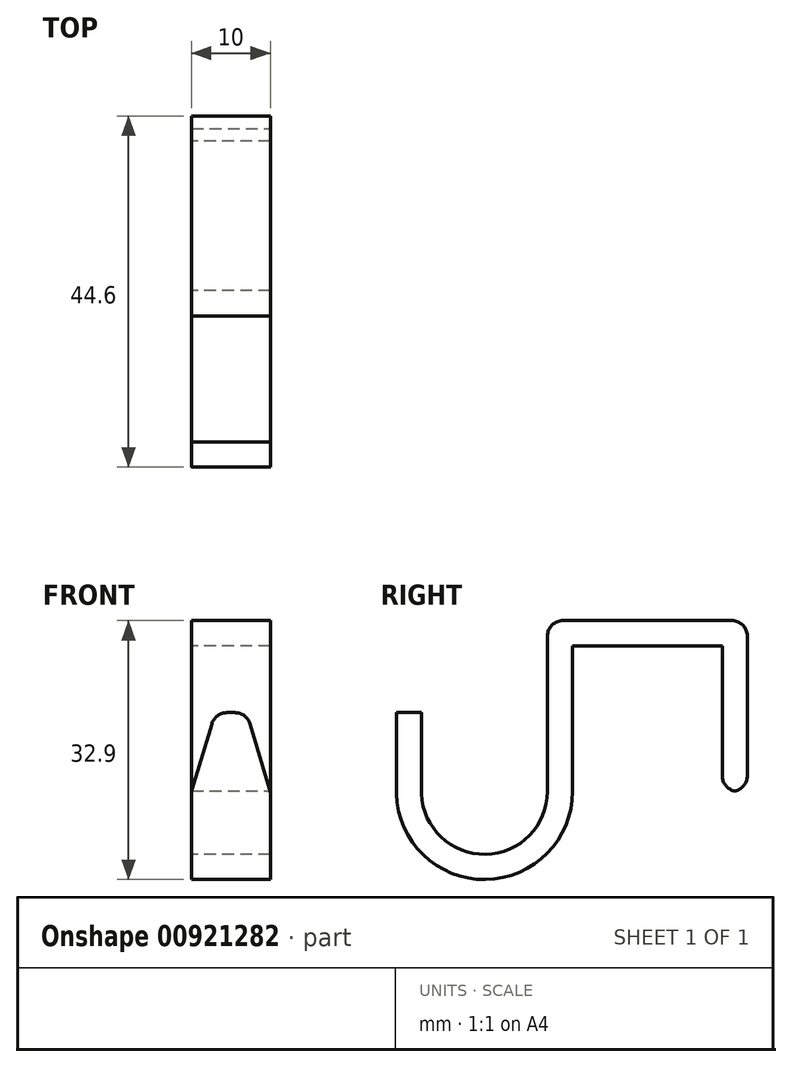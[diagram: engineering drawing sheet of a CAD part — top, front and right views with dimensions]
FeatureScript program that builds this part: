
annotation { "Feature Type Name" : "Feature", "Feature Type Description" : "" }
export const myFeature = defineFeature(function(context is Context, id is Id, definition is map)
    precondition{}
    {
        {
            var Q0;
            Q0=qCreatedBy(makeId("Right.planeOp"),FACE);
            var sketch = newSketch(context, id + "F0", { "sketchPlane" : qUnion([Q0])});
            skLineSegment(sketch, "E0.bottom", {"start": v(-12.7, 0) * mm, "end": v(12.7, 0) * mm});
            skLineSegment(sketch, "E0.top", {"start": v(-12.7, 21.7) * mm, "end": v(12.7, 21.7) * mm});
            skLineSegment(sketch, "E0.left", {"start": v(-12.7, 0) * mm, "end": v(-12.7, 21.7) * mm});
            skLineSegment(sketch, "E0.right", {"start": v(12.7, 0) * mm, "end": v(12.7, 21.7) * mm});
            skLineSegment(sketch, "E1.bottom", {"start": v(-9.5, 0) * mm, "end": v(9.5, 0) * mm});
            skLineSegment(sketch, "E1.top", {"start": v(-9.5, 18.5) * mm, "end": v(9.5, 18.5) * mm});
            skLineSegment(sketch, "E1.left", {"start": v(-9.5, 0) * mm, "end": v(-9.5, 18.5) * mm});
            skLineSegment(sketch, "E1.right", {"start": v(9.5, 0) * mm, "end": v(9.5, 18.5) * mm});
            skArc(sketch, "E2", {"start": v(-31.9, 0) * mm, "mid": v(-20.7, -11.2) * mm, "end": v(-9.5, 0) * mm});
            skArc(sketch, "E3", {"start": v(-28.7, 0) * mm, "mid": v(-20.7, -8) * mm, "end": v(-12.7, 0) * mm});
            skLineSegment(sketch, "E4", {"start": v(-31.9, 0) * mm, "end": v(-28.7, 0) * mm});
            skLineSegment(sketch, "E5.top", {"start": v(-31.9, 10) * mm, "end": v(-28.7, 10) * mm});
            skLineSegment(sketch, "E5.left", {"start": v(-31.9, 0) * mm, "end": v(-31.9, 10) * mm});
            skLineSegment(sketch, "E5.right", {"start": v(-28.7, 0) * mm, "end": v(-28.7, 10) * mm});
            skSolve(sketch);
        }
        {
            var Q0;
            Q0=makeQuery(id+"F0.imprint","IMPRINT",FACE,{"disambiguationData":[TD([[makeQuery(id+"F0.imprint","IMPRINT",EDGE,{"derivedFrom":sQuery(id+"F0.wireOp",EDGE,"E4")}),1.0]])]});
            var Q1;
            {var subQ2=sQuery(id+"F0.wireOp",EDGE,"E2");Q1=makeQuery(id+"F0.imprint","IMPRINT",FACE,{"disambiguationData":[TD([[makeQuery(id+"F0.imprint","IMPRINT",EDGE,{"derivedFrom":subQ2}),1.0]])]});}
            var Q2;
            Q2=makeQuery(id+"F0.imprint","IMPRINT",FACE,{"disambiguationData":[TD([[makeQuery(id+"F0.imprint","IMPRINT",EDGE,{"derivedFrom":sQuery(id+"F0.wireOp",EDGE,"E0.top")}),-1.0]])]});
            extrude(context, id + "F1", {"entities" : qUnion([Q0, Q1, Q2]), "depth" : 10 * mm, "offsetDistance" : 25 * mm});
        }
        {
            var Q0;
            Q0=makeQuery(id+"F1.opExtrude","CAP_EDGE",EDGE,{"disambiguationData":[OSD([sQuery(id+"F0.wireOp",EDGE,"E5.top")])],"isStart":false});
            var Q1;
            Q1=makeQuery(id+"F1.opExtrude","CAP_EDGE",EDGE,{"disambiguationData":[OSD([sQuery(id+"F0.wireOp",EDGE,"E5.top")])],"isStart":true});
            chamfer(context, id + "F2", {"entities" : qUnion([Q0, Q1]), "chamferType" : ChamferType.TWO_OFFSETS, "width1" : 3 * mm, "oppositeDirection" : false, "width2" : 10 * mm});
        }
        {
            var Q0;
            {var subQ0=sQuery(id+"F0.wireOp",EDGE,"E5.top");Q0=makeQuery(id+"F2.opChamfer","BLEND_EDGE",EDGE,{"blendedFrom":[makeQuery(id+"F1.opExtrude","CAP_EDGE",EDGE,{"disambiguationData":[OSD([subQ0])],"isStart":false}),makeQuery(id+"F1.opExtrude","SWEPT_FACE",FACE,{"disambiguationData":[OSD([subQ0])]})],"blendedInto":[makeQuery(id+"F1.opExtrude","SWEPT_FACE",FACE,{"disambiguationData":[OSD([subQ0])]})]});}
            var Q1;
            {var subQ0=sQuery(id+"F0.wireOp",EDGE,"E5.top");Q1=makeQuery(id+"F2.opChamfer","BLEND_EDGE",EDGE,{"blendedFrom":[makeQuery(id+"F1.opExtrude","CAP_EDGE",EDGE,{"disambiguationData":[OSD([subQ0])],"isStart":true}),makeQuery(id+"F1.opExtrude","SWEPT_FACE",FACE,{"disambiguationData":[OSD([subQ0])]})],"blendedInto":[makeQuery(id+"F1.opExtrude","SWEPT_FACE",FACE,{"disambiguationData":[OSD([subQ0])]})]});}
            var Q2;
            {var subQ0=sQuery(id+"F0.wireOp",EDGE,"E5.top");Q2=makeQuery(id+"F2.opChamfer","BLEND_EDGE",EDGE,{"blendedFrom":[makeQuery(id+"F1.opExtrude","CAP_EDGE",EDGE,{"disambiguationData":[OSD([subQ0])],"isStart":false}),makeQuery(id+"F1.opExtrude","CAP_FACE",FACE,{"disambiguationData":[OSD([sQuery(id+"F0.wireOp",EDGE,"E0.bottom"),sQuery(id+"F0.wireOp",EDGE,"E0.top"),sQuery(id+"F0.wireOp",EDGE,"E0.left"),sQuery(id+"F0.wireOp",EDGE,"E0.right"),sQuery(id+"F0.wireOp",EDGE,"E1.top"),sQuery(id+"F0.wireOp",EDGE,"E1.left"),sQuery(id+"F0.wireOp",EDGE,"E1.right"),sQuery(id+"F0.wireOp",EDGE,"E2"),sQuery(id+"F0.wireOp",EDGE,"E3"),subQ0,sQuery(id+"F0.wireOp",EDGE,"E5.left"),sQuery(id+"F0.wireOp",EDGE,"E5.right")])],"isStart":false})],"blendedInto":[makeQuery(id+"F1.opExtrude","CAP_FACE",FACE,{"disambiguationData":[OSD([sQuery(id+"F0.wireOp",EDGE,"E0.bottom"),sQuery(id+"F0.wireOp",EDGE,"E0.top"),sQuery(id+"F0.wireOp",EDGE,"E0.left"),sQuery(id+"F0.wireOp",EDGE,"E0.right"),sQuery(id+"F0.wireOp",EDGE,"E1.top"),sQuery(id+"F0.wireOp",EDGE,"E1.left"),sQuery(id+"F0.wireOp",EDGE,"E1.right"),sQuery(id+"F0.wireOp",EDGE,"E2"),sQuery(id+"F0.wireOp",EDGE,"E3"),subQ0,sQuery(id+"F0.wireOp",EDGE,"E5.left"),sQuery(id+"F0.wireOp",EDGE,"E5.right")])],"isStart":false})]});}
            var Q3;
            {var subQ0=sQuery(id+"F0.wireOp",EDGE,"E5.top");Q3=makeQuery(id+"F2.opChamfer","BLEND_EDGE",EDGE,{"blendedFrom":[makeQuery(id+"F1.opExtrude","CAP_EDGE",EDGE,{"disambiguationData":[OSD([subQ0])],"isStart":true}),makeQuery(id+"F1.opExtrude","CAP_FACE",FACE,{"disambiguationData":[OSD([sQuery(id+"F0.wireOp",EDGE,"E0.bottom"),sQuery(id+"F0.wireOp",EDGE,"E0.top"),sQuery(id+"F0.wireOp",EDGE,"E0.left"),sQuery(id+"F0.wireOp",EDGE,"E0.right"),sQuery(id+"F0.wireOp",EDGE,"E1.top"),sQuery(id+"F0.wireOp",EDGE,"E1.left"),sQuery(id+"F0.wireOp",EDGE,"E1.right"),sQuery(id+"F0.wireOp",EDGE,"E2"),sQuery(id+"F0.wireOp",EDGE,"E3"),subQ0,sQuery(id+"F0.wireOp",EDGE,"E5.left"),sQuery(id+"F0.wireOp",EDGE,"E5.right")])],"isStart":true})],"blendedInto":[makeQuery(id+"F1.opExtrude","CAP_FACE",FACE,{"disambiguationData":[OSD([sQuery(id+"F0.wireOp",EDGE,"E0.bottom"),sQuery(id+"F0.wireOp",EDGE,"E0.top"),sQuery(id+"F0.wireOp",EDGE,"E0.left"),sQuery(id+"F0.wireOp",EDGE,"E0.right"),sQuery(id+"F0.wireOp",EDGE,"E1.top"),sQuery(id+"F0.wireOp",EDGE,"E1.left"),sQuery(id+"F0.wireOp",EDGE,"E1.right"),sQuery(id+"F0.wireOp",EDGE,"E2"),sQuery(id+"F0.wireOp",EDGE,"E3"),subQ0,sQuery(id+"F0.wireOp",EDGE,"E5.left"),sQuery(id+"F0.wireOp",EDGE,"E5.right")])],"isStart":true})]});}
            var Q4;
            Q4=makeQuery(id+"F1.opExtrude","SWEPT_EDGE",EDGE,{"disambiguationData":[OSD([sQuery(id+"F0.wireOp",EDGE,"E0.top"),sQuery(id+"F0.wireOp",EDGE,"E0.left")])]});
            var Q5;
            Q5=makeQuery(id+"F1.opExtrude","SWEPT_EDGE",EDGE,{"disambiguationData":[OSD([sQuery(id+"F0.wireOp",EDGE,"E0.top"),sQuery(id+"F0.wireOp",EDGE,"E0.right")])]});
            var Q6;
            Q6=makeQuery(id+"F1.opExtrude","SWEPT_EDGE",EDGE,{"disambiguationData":[OSD([sQuery(id+"F0.wireOp",EDGE,"E0.bottom"),sQuery(id+"F0.wireOp",EDGE,"E1.bottom"),sQuery(id+"F0.wireOp",EDGE,"E1.right")])]});
            var Q7;
            Q7=makeQuery(id+"F1.opExtrude","SWEPT_EDGE",EDGE,{"disambiguationData":[OSD([sQuery(id+"F0.wireOp",EDGE,"E0.bottom"),sQuery(id+"F0.wireOp",EDGE,"E0.right")])]});
            fillet(context, id + "F3", {"entities" : qUnion([Q0, Q1, Q2, Q3, Q4, Q5, Q6, Q7]), "radius" : 2 * mm, "tangentPropagation" : true, "allowEdgeOverflow" : false});
        }
    });
